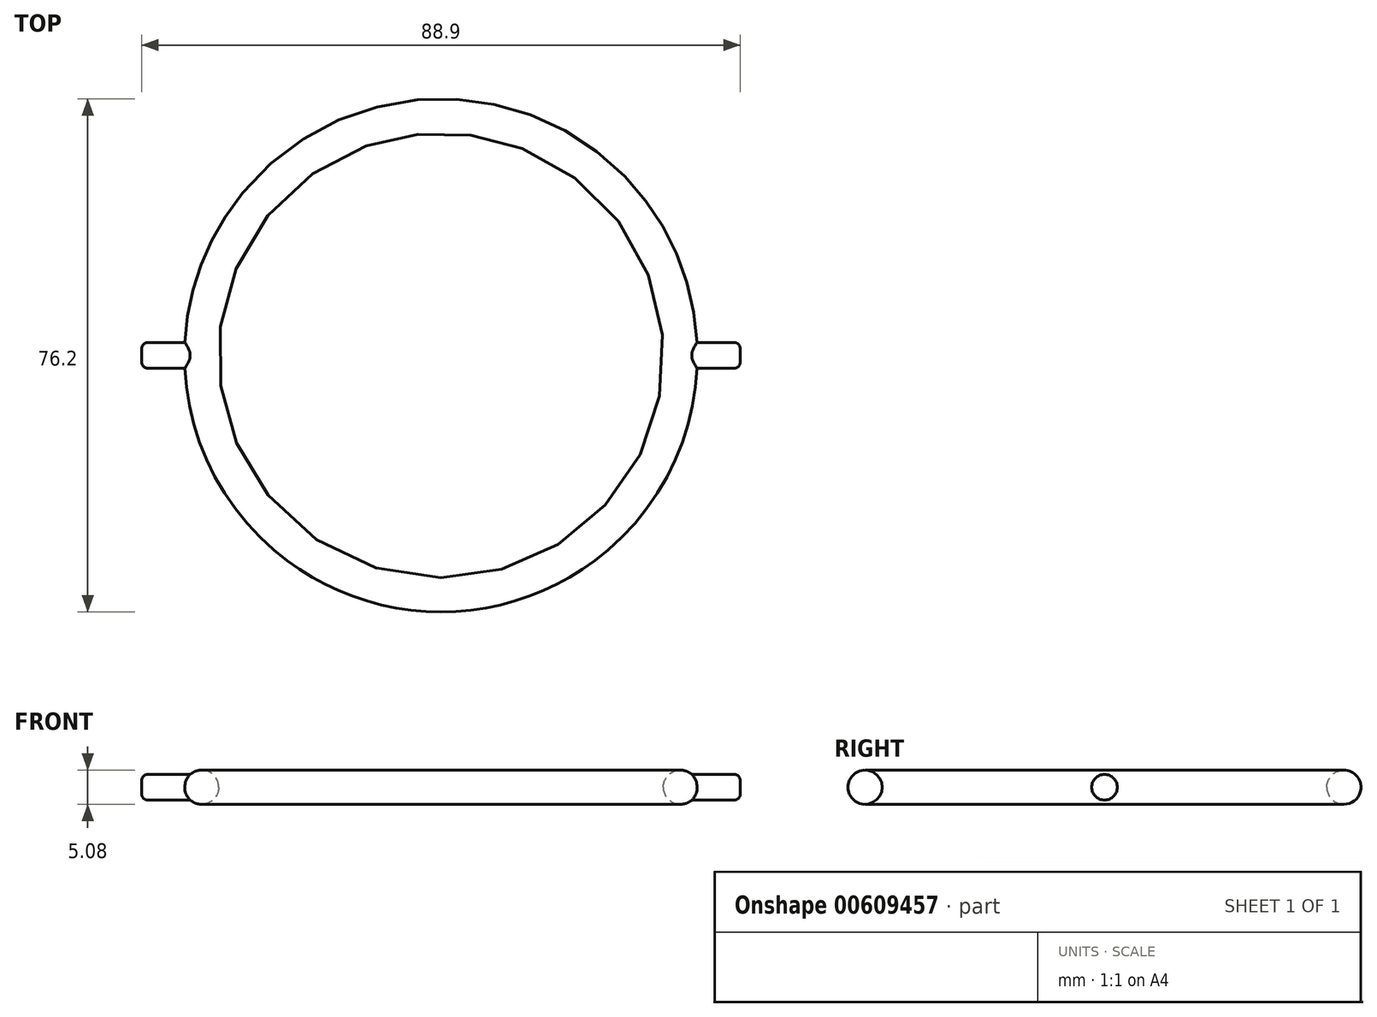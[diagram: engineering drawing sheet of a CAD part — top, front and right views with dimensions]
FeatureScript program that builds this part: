
annotation { "Feature Type Name" : "Feature", "Feature Type Description" : "" }
export const myFeature = defineFeature(function(context is Context, id is Id, definition is map)
    precondition{}
    {
        {
            var Q0;
            Q0=qCreatedBy(makeId("Top.planeOp"),FACE);
            var sketch = newSketch(context, id + "F0", { "sketchPlane" : qUnion([Q0])});
            skCircle(sketch, "E0", {"center": v(0, 0) * mm, "radius": 35.56 * mm});
            skSolve(sketch);
        }
        {
            var Q0;
            Q0=qCreatedBy(makeId("Right.planeOp"),FACE);
            var sketch = newSketch(context, id + "F1", { "sketchPlane" : qUnion([Q0])});
            skCircle(sketch, "E1", {"center": v(-35.56, 0) * mm, "radius": 2.54 * mm});
            skSolve(sketch);
        }
        {
            var Q0;
            Q0=makeQuery(id+"F1.imprint","IMPRINT",FACE,{"disambiguationData":[TD([[makeQuery(id+"F1.imprint","IMPRINT",EDGE,{"derivedFrom":sQuery(id+"F1.wireOp",EDGE,"E1")}),1.0]])]});
            var Q1;
            Q1=sQuery(id+"F0.wireOp",EDGE,"E0");
            sweep(context, id + "F2", {"profiles" : qUnion([Q0]), "path" : qUnion([Q1])});
        }
        {
            var Q0;
            Q0=qCreatedBy(makeId("Right.planeOp"),FACE);
            cPlane(context, id + "F3", {"entities" : qUnion([Q0]), "cplaneType" : CPlaneType.OFFSET, "offset" : 44.45 * mm, "width" : 152.4 * mm, "height" : 152.4 * mm});
        }
        {
            var Q0;
            Q0=qCreatedBy(id+"F3.planeOp",FACE);
            var sketch = newSketch(context, id + "F4", { "sketchPlane" : qUnion([Q0])});
            skCircle(sketch, "E2", {"center": v(0, 0) * mm, "radius": 1.9 * mm});
            skSolve(sketch);
        }
        {
            var Q0;
            Q0=makeQuery(id+"F4.imprint","IMPRINT",FACE,{"disambiguationData":[TD([[makeQuery(id+"F4.imprint","IMPRINT",EDGE,{"derivedFrom":sQuery(id+"F4.wireOp",EDGE,"E2")}),1.0]])]});
            extrude(context, id + "F5", {"entities" : qUnion([Q0]), "operationType" : NewBodyOperationType.ADD, "endBound" : BoundingType.UP_TO_NEXT, "oppositeDirection" : true, "depth" : 5.08 * mm, "offsetDistance" : 25.4 * mm});
        }
        {
            var Q0;
            Q0=makeQuery(id+"F5.opExtrude","CAP_EDGE",EDGE,{"disambiguationData":[OSD([sQuery(id+"F4.wireOp",EDGE,"E2")])],"isStart":true});
            fillet(context, id + "F6", {"entities" : qUnion([Q0]), "radius" : 0.89 * mm, "tangentPropagation" : true, "allowEdgeOverflow" : false});
        }
        {
            var Q0;
            Q0=makeQuery(id+"F2.opSweep","SWEPT_BODY",BODY,{"disambiguationData":[OSD([sQuery(id+"F0.wireOp",EDGE,"E0"),sQuery(id+"F1.wireOp",EDGE,"E1")])]});
            var Q1;
            Q1=qCreatedBy(makeId("Right.planeOp"),FACE);
            mirror(context, id + "F7", {"operationType" : NewBodyOperationType.ADD, "entities" : qUnion([Q0]), "mirrorPlane" : qUnion([Q1])});
        }
    });
